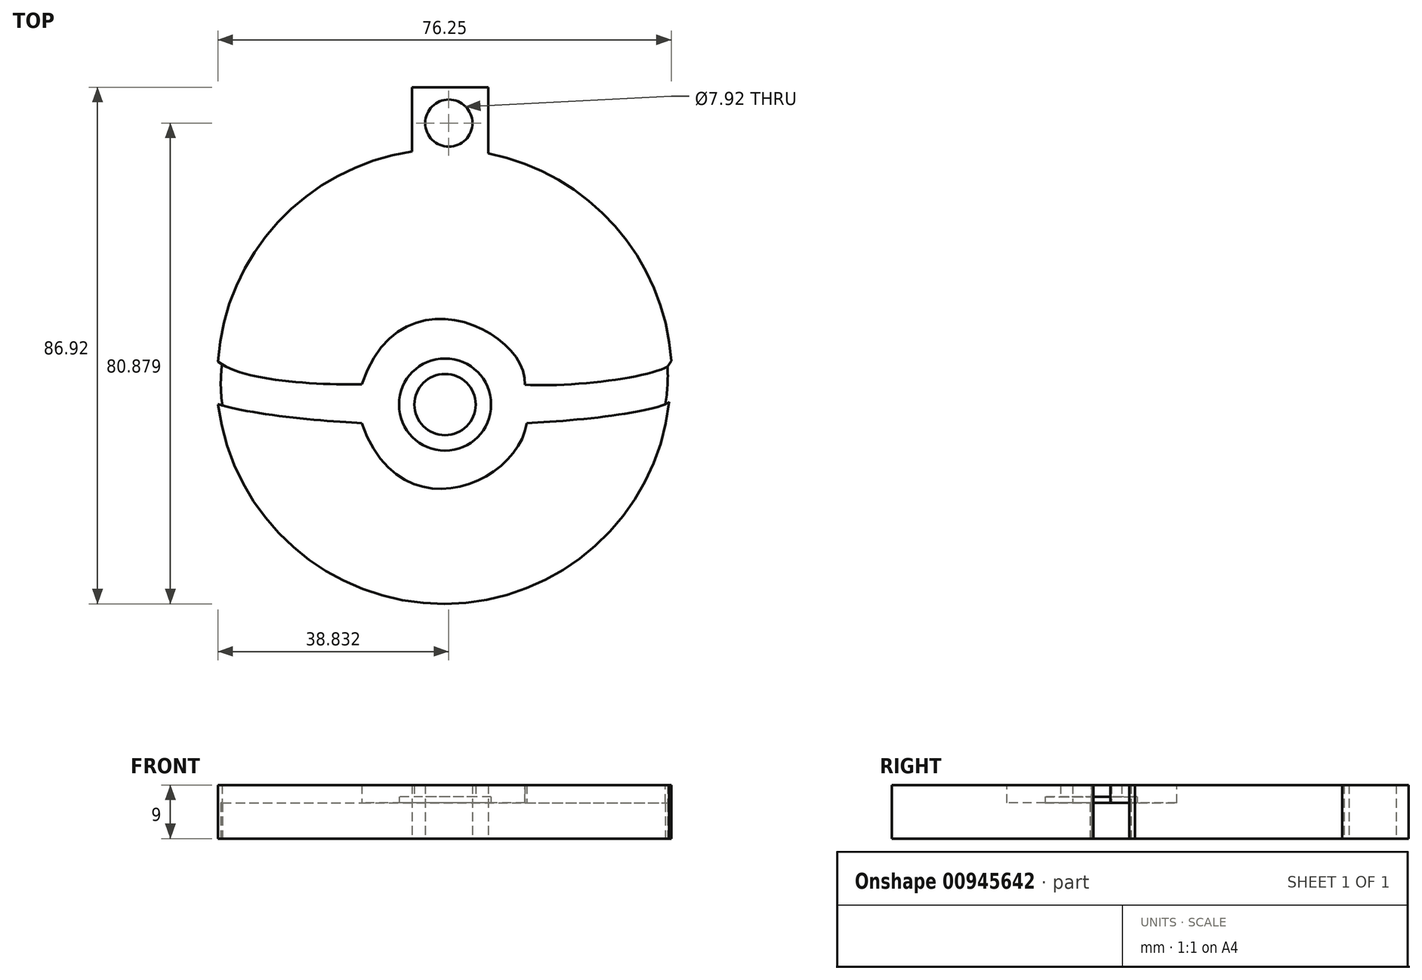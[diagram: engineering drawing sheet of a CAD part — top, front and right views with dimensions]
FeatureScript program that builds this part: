
annotation { "Feature Type Name" : "Feature", "Feature Type Description" : "" }
export const myFeature = defineFeature(function(context is Context, id is Id, definition is map)
    precondition{}
    {
        {
            var Q0;
            Q0=qCreatedBy(makeId("Top.planeOp"),FACE);
            var sketch = newSketch(context, id + "F0", { "sketchPlane" : qUnion([Q0])});
            skCircle(sketch, "E0", {"center": v(-53.8, -17.74) * mm, "radius": 5.15 * mm});
            skFitSpline(sketch, "E1", {"points": [v(-67.8, -20.84) * mm, v(-40.05, -20.84) * mm], "startDerivative": vector(19.46, -56.14) * mm, "endDerivative": vector(4.53, 30.62) * mm});
            skFitSpline(sketch, "E2", {"points": [v(-40.4, -14.38) * mm, v(-67.8, -14.3) * mm], "startDerivative": vector(2.02, 26.4) * mm, "endDerivative": vector(-19.94, -58.86) * mm});
            skLineSegment(sketch, "E3", {"start": v(-40.4, -14.38) * mm, "end": v(-40.05, -20.84) * mm});
            skLineSegment(sketch, "E4", {"start": v(-67.8, -14.3) * mm, "end": v(-67.8, -20.84) * mm});
            skArc(sketch, "E5", {"start": v(-15.75, -10.39) * mm, "mid": v(-53.92, 25.22) * mm, "end": v(-92, -10.5) * mm});
            skFitSpline(sketch, "E6", {"points": [v(-40.4, -14.38) * mm, v(-15.75, -10.39) * mm], "startDerivative": vector(24.53, -1.78) * mm, "endDerivative": vector(-1.75, 7.13) * mm});
            skFitSpline(sketch, "E7", {"points": [v(-92, -10.5) * mm, v(-67.8, -14.3) * mm], "startDerivative": vector(12.47, -9.9) * mm, "endDerivative": vector(23.79, 0.46) * mm});
            skFitSpline(sketch, "E8", {"points": [v(-91.98, -17.66) * mm, v(-67.8, -20.84) * mm], "startDerivative": vector(12.91, -4.7) * mm, "endDerivative": vector(19.34, -0.64) * mm});
            skFitSpline(sketch, "E9", {"points": [v(-40.05, -20.84) * mm, v(-16.09, -17.33) * mm], "startDerivative": vector(20.79, 0.76) * mm, "endDerivative": vector(9.19, 5.77) * mm});
            skArc(sketch, "E10", {"start": v(-91.98, -17.66) * mm, "mid": v(-53.88, -51.26) * mm, "end": v(-16.09, -17.33) * mm});
            skCircle(sketch, "E11", {"center": v(-53.8, -17.74) * mm, "radius": 7.74 * mm});
            skArc(sketch, "E12", {"start": v(-16.76, -17.67) * mm, "mid": v(-16.38, -14.5) * mm, "end": v(-16.4, -11.32) * mm});
            skArc(sketch, "E13", {"start": v(-91.32, -10.97) * mm, "mid": v(-91.52, -14.44) * mm, "end": v(-91.24, -17.9) * mm});
            skLineSegment(sketch, "E14", {"start": v(-92, -10.5) * mm, "end": v(-91.32, -10.97) * mm});
            skLineSegment(sketch, "E15", {"start": v(-91.24, -17.9) * mm, "end": v(-91.98, -17.66) * mm});
            skLineSegment(sketch, "E16", {"start": v(-16.4, -11.32) * mm, "end": v(-15.75, -10.39) * mm});
            skLineSegment(sketch, "E17", {"start": v(-16.76, -17.67) * mm, "end": v(-16.09, -17.33) * mm});
            skLineSegment(sketch, "E18.bottom", {"start": v(-59.36, 23.28) * mm, "end": v(-46.53, 23.28) * mm});
            skLineSegment(sketch, "E18.top", {"start": v(-59.36, 35.66) * mm, "end": v(-46.53, 35.66) * mm});
            skLineSegment(sketch, "E18.left", {"start": v(-59.36, 23.28) * mm, "end": v(-59.36, 35.66) * mm});
            skLineSegment(sketch, "E18.right", {"start": v(-46.53, 23.28) * mm, "end": v(-46.53, 35.66) * mm});
            skCircle(sketch, "E19", {"center": v(-53.17, 29.62) * mm, "radius": 3.96 * mm});
            skSolve(sketch);
        }
        {
            var Q0;
            Q0=makeQuery(id+"F0.imprint","IMPRINT",FACE,{"disambiguationData":[TD([[makeQuery(id+"F0.imprint","IMPRINT",EDGE,{"derivedFrom":sQuery(id+"F0.wireOp",EDGE,"E2")}),-1.0]])]});
            var Q1;
            Q1=makeQuery(id+"F0.imprint","IMPRINT",FACE,{"disambiguationData":[TD([[makeQuery(id+"F0.imprint","IMPRINT",EDGE,{"derivedFrom":sQuery(id+"F0.wireOp",EDGE,"E1")}),-1.0]])]});
            var Q2;
            Q2=makeQuery(id+"F0.imprint","IMPRINT",FACE,{"disambiguationData":[TD([[makeQuery(id+"F0.imprint","IMPRINT",EDGE,{"derivedFrom":sQuery(id+"F0.wireOp",EDGE,"E0")}),1.0]])]});
            var Q3;
            {var subQ1=sQuery(id+"F0.wireOp",EDGE,"E18.top");Q3=makeQuery(id+"F0.imprint","IMPRINT",FACE,{"disambiguationData":[TD([[makeQuery(id+"F0.imprint","IMPRINT",EDGE,{"derivedFrom":subQ1}),-1.0]])]});}
            var Q4;
            {var subQ5=sQuery(id+"F0.wireOp",EDGE,"E18.bottom");Q4=makeQuery(id+"F0.imprint","IMPRINT",FACE,{"disambiguationData":[TD([[makeQuery(id+"F0.imprint","IMPRINT",EDGE,{"derivedFrom":subQ5}),1.0]])]});}
            extrude(context, id + "F1", {"entities" : qUnion([Q0, Q1, Q2, Q3, Q4]), "depth" : 9 * mm, "offsetDistance" : 25 * mm});
        }
        {
            var Q0;
            {var subQ0=sQuery(id+"F0.wireOp",EDGE,"E4");Q0=makeQuery(id+"F0.imprint","IMPRINT",FACE,{"disambiguationData":[TD([[makeQuery(id+"F0.imprint","IMPRINT",EDGE,{"derivedFrom":subQ0}),-1.0]])]});}
            var Q1;
            {var subQ0=sQuery(id+"F0.wireOp",EDGE,"E3");Q1=makeQuery(id+"F0.imprint","IMPRINT",FACE,{"disambiguationData":[TD([[makeQuery(id+"F0.imprint","IMPRINT",EDGE,{"derivedFrom":subQ0}),1.0]])]});}
            var Q2;
            Q2=makeQuery(id+"F0.imprint","IMPRINT",FACE,{"disambiguationData":[TD([[makeQuery(id+"F0.imprint","IMPRINT",EDGE,{"derivedFrom":sQuery(id+"F0.wireOp",EDGE,"E1")}),1.0]])]});
            extrude(context, id + "F2", {"entities" : qUnion([Q0, Q1, Q2]), "operationType" : NewBodyOperationType.ADD, "depth" : 6 * mm, "offsetDistance" : 25 * mm});
        }
        {
            var Q0;
            Q0=makeQuery(id+"F0.imprint","IMPRINT",FACE,{"disambiguationData":[TD([[makeQuery(id+"F0.imprint","IMPRINT",EDGE,{"derivedFrom":sQuery(id+"F0.wireOp",EDGE,"E0")}),-1.0]])]});
            extrude(context, id + "F3", {"entities" : qUnion([Q0]), "operationType" : NewBodyOperationType.ADD, "depth" : 7 * mm, "offsetDistance" : 25 * mm});
        }
    });
